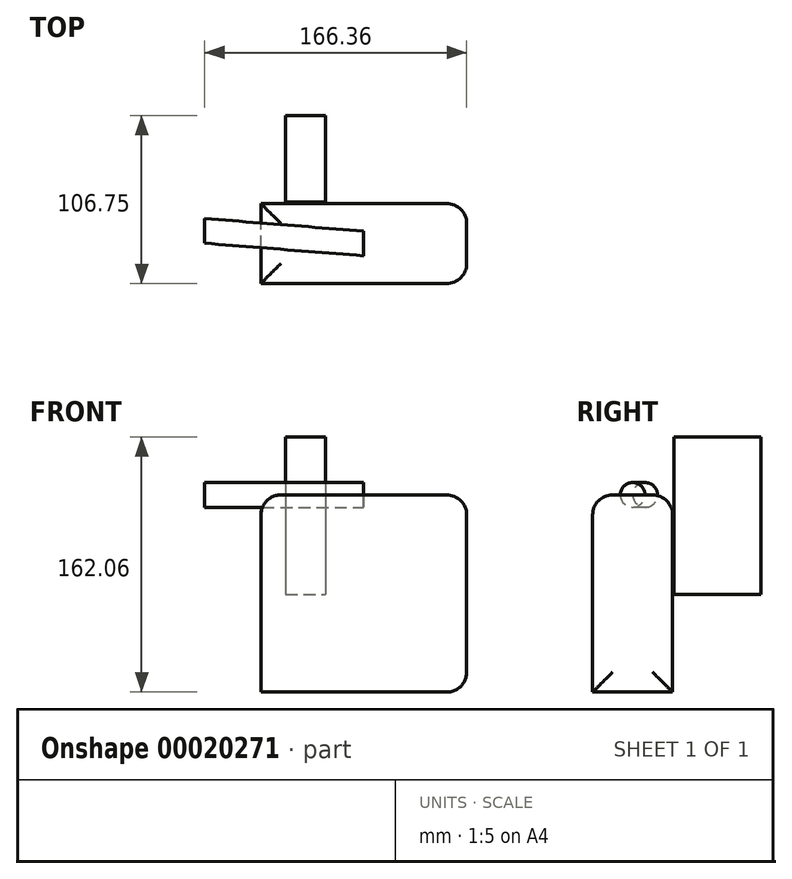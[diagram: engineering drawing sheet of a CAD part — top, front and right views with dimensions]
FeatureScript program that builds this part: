
annotation { "Feature Type Name" : "Feature", "Feature Type Description" : "" }
export const myFeature = defineFeature(function(context is Context, id is Id, definition is map)
    precondition{}
    {
        {
            var Q0;
            Q0=qCreatedBy(makeId("Front.planeOp"),FACE);
            var sketch = newSketch(context, id + "F0", { "sketchPlane" : qUnion([Q0])});
            skLineSegment(sketch, "E0.bottom", {"start": v(-65.19, 63.18) * mm, "end": v(65.53, 63.18) * mm});
            skLineSegment(sketch, "E0.top", {"start": v(-65.19, -62.06) * mm, "end": v(65.53, -62.06) * mm});
            skLineSegment(sketch, "E0.left", {"start": v(-65.19, 63.18) * mm, "end": v(-65.19, -62.06) * mm});
            skLineSegment(sketch, "E0.right", {"start": v(65.53, 63.18) * mm, "end": v(65.53, -62.06) * mm});
            skSolve(sketch);
        }
        {
            var Q0;
            Q0=makeQuery(id+"F0.imprint","IMPRINT",FACE,{"disambiguationData":[TD([[makeQuery(id+"F0.imprint","IMPRINT",EDGE,{"derivedFrom":sQuery(id+"F0.wireOp",EDGE,"E0.bottom")}),-1.0]])]});
            extrude(context, id + "F1", {"entities" : qUnion([Q0]), "depth" : 25.4 * mm, "hasSecondDirection" : true, "secondDirectionOppositeDirection" : true, "secondDirectionDepth" : 25.4 * mm});
        }
        {
            var Q0;
            Q0=makeQuery(id+"F1.opExtrude","CAP_EDGE",EDGE,{"disambiguationData":[OSD([sQuery(id+"F0.wireOp",EDGE,"E0.bottom")])],"isStart":false});
            var Q1;
            Q1=makeQuery(id+"F1.opExtrude","SWEPT_FACE",FACE,{"disambiguationData":[OSD([sQuery(id+"F0.wireOp",EDGE,"E0.right")])]});
            var Q2;
            Q2=makeQuery(id+"F1.opExtrude","SWEPT_FACE",FACE,{"disambiguationData":[OSD([sQuery(id+"F0.wireOp",EDGE,"E0.bottom")])]});
            fillet(context, id + "F2", {"entities" : qUnion([Q0, Q1, Q2]), "radius" : 12.7 * mm, "tangentPropagation" : true, "allowEdgeOverflow" : false});
        }
        {
            var Q0;
            Q0=makeQuery(id+"F1.opExtrude","SWEPT_FACE",FACE,{"disambiguationData":[OSD([sQuery(id+"F0.wireOp",EDGE,"E0.bottom")])]});
            var sketch = newSketch(context, id + "F3", { "sketchPlane" : qUnion([Q0])});
            skLineSegment(sketch, "E1", {"start": v(0, 0) * mm, "end": v(-100.83, 8) * mm});
            skLineSegment(sketch, "E2", {"start": v(-106.37, 12.35) * mm, "end": v(-114.53, 37.28) * mm});
            skLineSegment(sketch, "E3", {"start": v(-113.64, 42.98) * mm, "end": v(-84.89, 82.7) * mm});
            skLineSegment(sketch, "E4", {"start": v(-82.2, 84.83) * mm, "end": v(12.7, 124.54) * mm});
            skLineSegment(sketch, "E5", {"start": v(12.7, 124.54) * mm, "end": v(45.63, 114.8) * mm});
            skLineSegment(sketch, "E6", {"start": v(45.63, 114.8) * mm, "end": v(81.62, 96.42) * mm});
            skLineSegment(sketch, "E7", {"start": v(81.62, 96.42) * mm, "end": v(94.88, 105.65) * mm});
            skPoint(sketch, "E8.visualSharp", {"position": v(-105.05, 8.33) * mm});
            skArc(sketch, "E8.filletArc", {"start": v(-106.37, 12.35) * mm, "mid": v(-104.26, 9.34) * mm, "end": v(-100.83, 8) * mm});
            skPoint(sketch, "E9.visualSharp", {"position": v(-115.54, 40.36) * mm});
            skArc(sketch, "E9.filletArc", {"start": v(-113.64, 42.98) * mm, "mid": v(-114.77, 40.24) * mm, "end": v(-114.53, 37.28) * mm});
            skPoint(sketch, "E10.visualSharp", {"position": v(-83.84, 84.14) * mm});
            skArc(sketch, "E10.filletArc", {"start": v(-82.2, 84.83) * mm, "mid": v(-83.7, 83.95) * mm, "end": v(-84.89, 82.7) * mm});
            skSolve(sketch);
        }
        {
            var Q0;
            Q0=qCreatedBy(makeId("Right.planeOp"),FACE);
            var sketch = newSketch(context, id + "F4", { "sketchPlane" : qUnion([Q0])});
            skCircle(sketch, "E11", {"center": v(0, 63.18) * mm, "radius": 7.84 * mm});
            skSolve(sketch);
        }
        {
            var Q0;
            Q0=makeQuery(id+"F4.imprint","IMPRINT",FACE,{"disambiguationData":[TD([[makeQuery(id+"F4.imprint","IMPRINT",EDGE,{"derivedFrom":sQuery(id+"F4.wireOp",EDGE,"E11")}),1.0]])]});
            var Q1;
            Q1=sQuery(id+"F3.wireOp",EDGE,"E1");
            sweep(context, id + "F5", {"profiles" : qUnion([Q0]), "path" : qUnion([Q1])});
        }
        {
            var Q0;
            Q0=qCreatedBy(makeId("Top.planeOp"),FACE);
            var sketch = newSketch(context, id + "F6", { "sketchPlane" : qUnion([Q0])});
            skLineSegment(sketch, "E12.bottom", {"start": v(-49.5, 26.35) * mm, "end": v(-24.1, 26.35) * mm});
            skLineSegment(sketch, "E12.top", {"start": v(-49.5, 81.35) * mm, "end": v(-24.1, 81.35) * mm});
            skLineSegment(sketch, "E12.left", {"start": v(-49.5, 26.35) * mm, "end": v(-49.5, 81.35) * mm});
            skLineSegment(sketch, "E12.right", {"start": v(-24.1, 26.35) * mm, "end": v(-24.1, 81.35) * mm});
            skSolve(sketch);
        }
        {
            var Q0;
            Q0=makeQuery(id+"F6.imprint","IMPRINT",FACE,{"disambiguationData":[TD([[makeQuery(id+"F6.imprint","IMPRINT",EDGE,{"derivedFrom":sQuery(id+"F6.wireOp",EDGE,"E12.bottom")}),1.0]])]});
            extrude(context, id + "F7", {"entities" : qUnion([Q0]), "depth" : 100 * mm});
        }
    });
